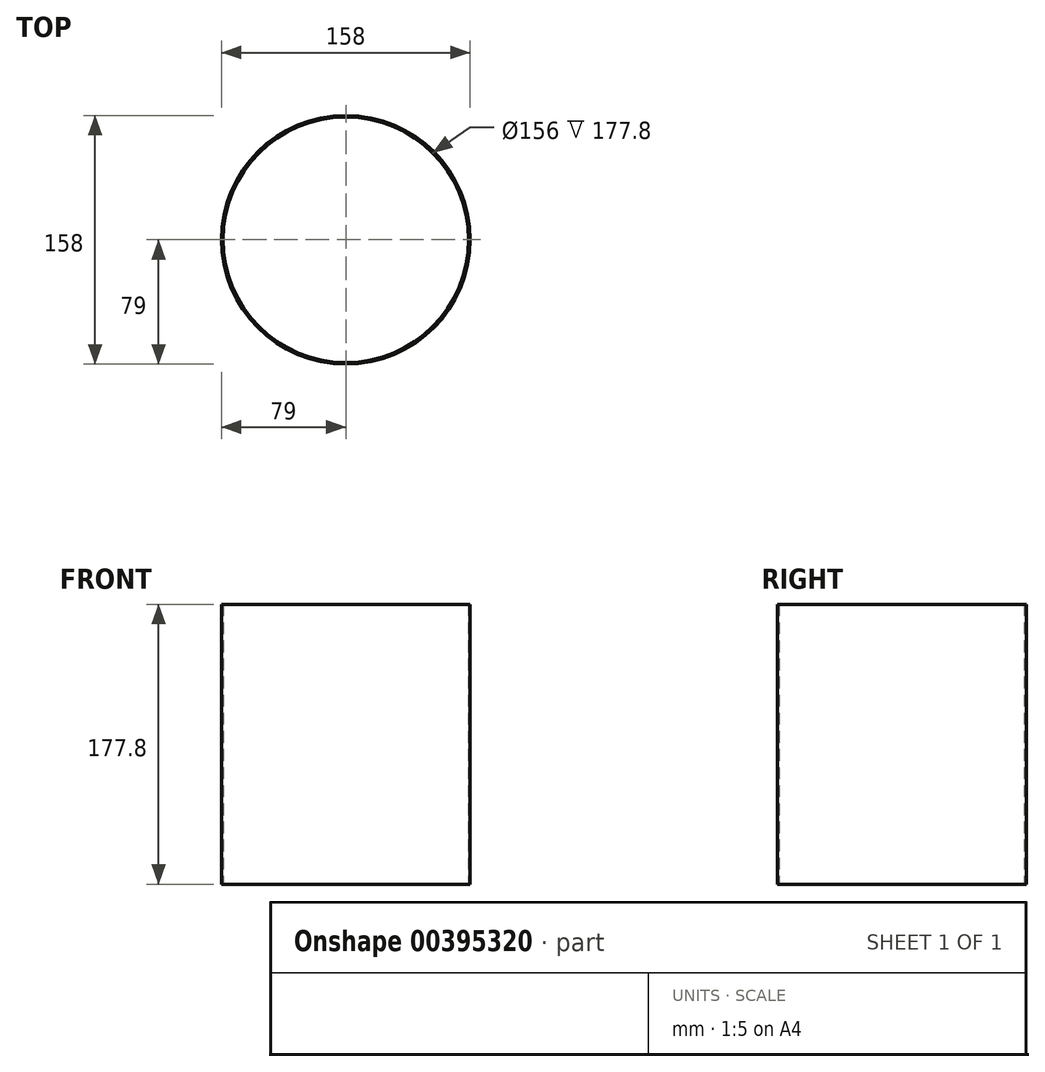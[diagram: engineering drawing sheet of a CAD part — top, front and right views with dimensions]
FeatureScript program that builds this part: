
annotation { "Feature Type Name" : "Feature", "Feature Type Description" : "" }
export const myFeature = defineFeature(function(context is Context, id is Id, definition is map)
    precondition{}
    {
        {
            var Q0;
            Q0=qCreatedBy(makeId("Top.planeOp"),FACE);
            var sketch = newSketch(context, id + "F0", { "sketchPlane" : qUnion([Q0])});
            skCircle(sketch, "E0", {"center": v(0, 0) * mm, "radius": 79 * mm});
            skSolve(sketch);
        }
        {
            var Q0;
            Q0=makeQuery(id+"F0.imprint","IMPRINT",FACE,{"disambiguationData":[TD([[makeQuery(id+"F0.imprint","IMPRINT",EDGE,{"derivedFrom":sQuery(id+"F0.wireOp",EDGE,"E0")}),1.0]])]});
            extrude(context, id + "F1", {"entities" : qUnion([Q0]), "depth" : 177.8 * mm});
        }
        {
            var Q0;
            Q0=makeQuery(id+"F1.opExtrude","CAP_FACE",FACE,{"disambiguationData":[OSD([sQuery(id+"F0.wireOp",EDGE,"E0")])],"isStart":false});
            shell(context, id + "F2", {"entities" : qUnion([Q0]), "thickness" : 1 * mm});
        }
        {
            var Q0;
            {var subQ0=sQuery(id+"F0.wireOp",EDGE,"E0");Q0=makeQuery(id+"F2.opShell","OFFSET_FACE",FACE,{"disambiguationData":[OSD([subQ0]),TDD([makeQuery(id+"F1.opExtrude","CAP_FACE",FACE,{"disambiguationData":[OSD([subQ0])],"isStart":true})])]});}
            extrude(context, id + "F3", {"entities" : qUnion([Q0]), "operationType" : NewBodyOperationType.REMOVE, "endBound" : BoundingType.THROUGH_ALL, "oppositeDirection" : true, "depth" : 25 * mm});
        }
        {
            var Q0;
            Q0=qCreatedBy(makeId("Top.planeOp"),FACE);
            var sketch = newSketch(context, id + "F4", { "sketchPlane" : qUnion([Q0])});
            skCircle(sketch, "E1", {"center": v(-59.23, 59.67) * mm, "radius": 2 * mm});
            skSolve(sketch);
        }
        {
            var Q0;
            Q0=makeQuery(id+"F4.imprint","IMPRINT",FACE,{"disambiguationData":[TD([[makeQuery(id+"F4.imprint","IMPRINT",EDGE,{"derivedFrom":sQuery(id+"F4.wireOp",EDGE,"E1")}),1.0]])]});
            extrude(context, id + "F5", {"entities" : qUnion([Q0]), "depth" : 110 * mm});
        }
        {
            var Q0;
            Q0=makeQuery(id+"F5.opExtrude","SWEPT_BODY",BODY,{"disambiguationData":[OSD([sQuery(id+"F4.wireOp",EDGE,"E1")])]});
            deleteBodies(context, id + "F6", {"entities" : qUnion([Q0])});
        }
    });
